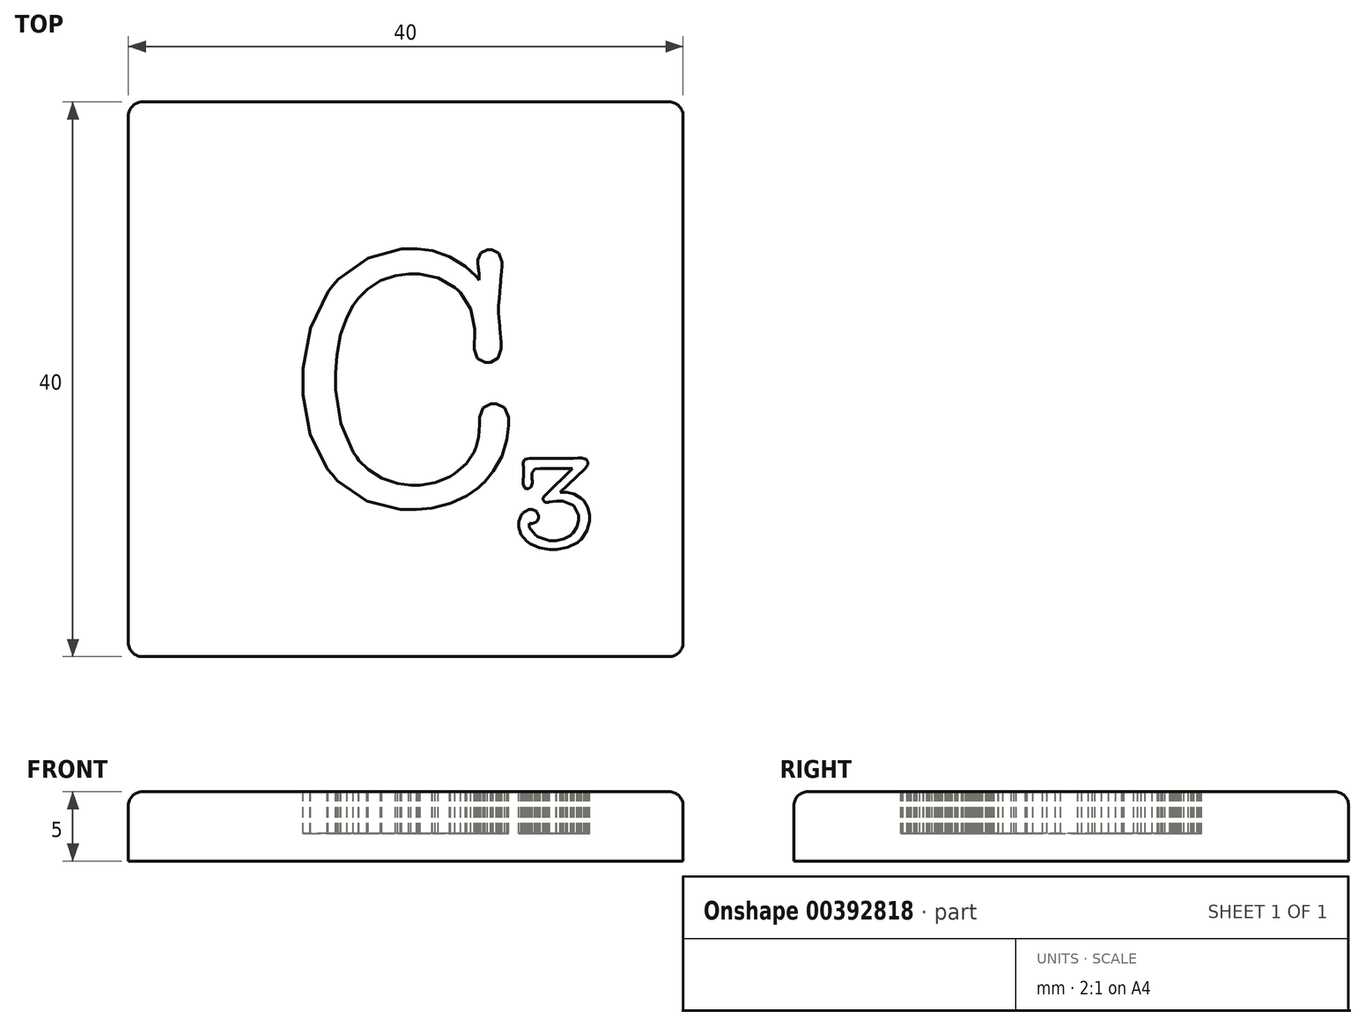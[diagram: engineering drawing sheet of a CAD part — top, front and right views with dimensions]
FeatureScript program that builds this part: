
annotation { "Feature Type Name" : "Feature", "Feature Type Description" : "" }
export const myFeature = defineFeature(function(context is Context, id is Id, definition is map)
    precondition{}
    {
        {
            var Q0;
            Q0=qCreatedBy(makeId("Top.planeOp"),FACE);
            var sketch = newSketch(context, id + "F0", { "sketchPlane" : qUnion([Q0])});
            skLineSegment(sketch, "E0.bottom", {"start": v(20, -20) * mm, "end": v(-20, -20) * mm});
            skLineSegment(sketch, "E0.top", {"start": v(20, 20) * mm, "end": v(-20, 20) * mm});
            skLineSegment(sketch, "E0.left", {"start": v(20, -20) * mm, "end": v(20, 20) * mm});
            skLineSegment(sketch, "E0.right", {"start": v(-20, -20) * mm, "end": v(-20, 20) * mm});
            skPoint(sketch, "E0.middle", {"position": v(0, 0) * mm});
            skSolve(sketch);
        }
        {
            var Q0;
            Q0=makeQuery(id+"F0.imprint","IMPRINT",FACE,{"disambiguationData":[TD([[makeQuery(id+"F0.imprint","IMPRINT",EDGE,{"derivedFrom":sQuery(id+"F0.wireOp",EDGE,"E0.bottom")}),-1.0]])]});
            extrude(context, id + "F1", {"entities" : qUnion([Q0]), "depth" : -5 * mm});
        }
        {
            var Q0;
            Q0=makeQuery(id+"F1.opExtrude","CAP_FACE",FACE,{"disambiguationData":[OSD([sQuery(id+"F0.wireOp",EDGE,"E0.bottom"),sQuery(id+"F0.wireOp",EDGE,"E0.top"),sQuery(id+"F0.wireOp",EDGE,"E0.left"),sQuery(id+"F0.wireOp",EDGE,"E0.right")])],"isStart":true});
            var Q1;
            Q1=makeQuery(id+"F1.opExtrude","SWEPT_EDGE",EDGE,{"disambiguationData":[OSD([sQuery(id+"F0.wireOp",EDGE,"E0.top"),sQuery(id+"F0.wireOp",EDGE,"E0.right")])]});
            var Q2;
            Q2=makeQuery(id+"F1.opExtrude","SWEPT_EDGE",EDGE,{"disambiguationData":[OSD([sQuery(id+"F0.wireOp",EDGE,"E0.top"),sQuery(id+"F0.wireOp",EDGE,"E0.left")])]});
            var Q3;
            Q3=makeQuery(id+"F1.opExtrude","SWEPT_EDGE",EDGE,{"disambiguationData":[OSD([sQuery(id+"F0.wireOp",EDGE,"E0.bottom"),sQuery(id+"F0.wireOp",EDGE,"E0.right")])]});
            var Q4;
            Q4=makeQuery(id+"F1.opExtrude","SWEPT_EDGE",EDGE,{"disambiguationData":[OSD([sQuery(id+"F0.wireOp",EDGE,"E0.bottom"),sQuery(id+"F0.wireOp",EDGE,"E0.left")])]});
            fillet(context, id + "F2", {"entities" : qUnion([Q0, Q1, Q2, Q3, Q4]), "radius" : 1 * mm, "tangentPropagation" : true, "allowEdgeOverflow" : false});
        }
        {
            var Q0;
            Q0=qCreatedBy(makeId("Top.planeOp"),FACE);
            var sketch = newSketch(context, id + "F3", { "sketchPlane" : qUnion([Q0])});
            skLineSegment(sketch, "E1", {"start": v(0.52, 9.4) * mm, "end": v(0.87, 9.4) * mm});
            skLineSegment(sketch, "E2", {"start": v(0.87, 9.4) * mm, "end": v(1.92, 9.27) * mm});
            skLineSegment(sketch, "E3", {"start": v(1.92, 9.27) * mm, "end": v(3.18, 8.84) * mm});
            skLineSegment(sketch, "E4", {"start": v(3.18, 8.84) * mm, "end": v(4.3, 8.14) * mm});
            skLineSegment(sketch, "E5", {"start": v(4.3, 8.14) * mm, "end": v(5.08, 7.43) * mm});
            skLineSegment(sketch, "E6", {"start": v(5.08, 7.43) * mm, "end": v(5.3, 7.16) * mm});
            skLineSegment(sketch, "E7", {"start": v(5.3, 7.16) * mm, "end": v(5.28, 7.45) * mm});
            skLineSegment(sketch, "E8", {"start": v(5.28, 7.45) * mm, "end": v(5.28, 7.74) * mm});
            skLineSegment(sketch, "E9", {"start": v(5.28, 7.74) * mm, "end": v(5.27, 7.77) * mm});
            skLineSegment(sketch, "E10", {"start": v(5.27, 7.77) * mm, "end": v(5.25, 7.89) * mm});
            skLineSegment(sketch, "E11", {"start": v(5.25, 7.89) * mm, "end": v(5.25, 7.92) * mm});
            skLineSegment(sketch, "E12", {"start": v(5.25, 7.92) * mm, "end": v(5.24, 8.02) * mm});
            skLineSegment(sketch, "E13", {"start": v(5.24, 8.02) * mm, "end": v(5.2, 8.45) * mm});
            skLineSegment(sketch, "E14", {"start": v(5.2, 8.45) * mm, "end": v(5.2, 8.62) * mm});
            skLineSegment(sketch, "E15", {"start": v(5.2, 8.62) * mm, "end": v(5.4, 9.13) * mm});
            skLineSegment(sketch, "E16", {"start": v(5.4, 9.13) * mm, "end": v(5.88, 9.35) * mm});
            skLineSegment(sketch, "E17", {"start": v(5.88, 9.35) * mm, "end": v(6.04, 9.35) * mm});
            skLineSegment(sketch, "E18", {"start": v(6.04, 9.35) * mm, "end": v(6.21, 9.35) * mm});
            skLineSegment(sketch, "E19", {"start": v(6.21, 9.35) * mm, "end": v(6.72, 9.08) * mm});
            skLineSegment(sketch, "E20", {"start": v(6.72, 9.08) * mm, "end": v(6.94, 8.45) * mm});
            skLineSegment(sketch, "E21", {"start": v(6.94, 8.45) * mm, "end": v(6.94, 8.24) * mm});
            skLineSegment(sketch, "E22", {"start": v(6.94, 8.24) * mm, "end": v(6.94, 8.14) * mm});
            skLineSegment(sketch, "E23", {"start": v(6.94, 8.14) * mm, "end": v(6.92, 7.82) * mm});
            skLineSegment(sketch, "E24", {"start": v(6.92, 7.82) * mm, "end": v(6.86, 7.15) * mm});
            skLineSegment(sketch, "E25", {"start": v(6.86, 7.15) * mm, "end": v(6.84, 6.97) * mm});
            skLineSegment(sketch, "E26", {"start": v(6.84, 6.97) * mm, "end": v(6.82, 6.75) * mm});
            skLineSegment(sketch, "E27", {"start": v(6.82, 6.75) * mm, "end": v(6.74, 5.85) * mm});
            skLineSegment(sketch, "E28", {"start": v(6.74, 5.85) * mm, "end": v(6.7, 5.32) * mm});
            skLineSegment(sketch, "E29", {"start": v(6.7, 5.32) * mm, "end": v(6.7, 5.15) * mm});
            skLineSegment(sketch, "E30", {"start": v(6.7, 5.15) * mm, "end": v(6.7, 4.78) * mm});
            skLineSegment(sketch, "E31", {"start": v(6.7, 4.78) * mm, "end": v(6.77, 3.82) * mm});
            skLineSegment(sketch, "E32", {"start": v(6.77, 3.82) * mm, "end": v(6.79, 3.7) * mm});
            skLineSegment(sketch, "E33", {"start": v(6.79, 3.7) * mm, "end": v(6.9, 2.69) * mm});
            skLineSegment(sketch, "E34", {"start": v(6.9, 2.69) * mm, "end": v(6.9, 2.42) * mm});
            skLineSegment(sketch, "E35", {"start": v(6.9, 2.42) * mm, "end": v(6.9, 2.2) * mm});
            skLineSegment(sketch, "E36", {"start": v(6.9, 2.2) * mm, "end": v(6.65, 1.53) * mm});
            skLineSegment(sketch, "E37", {"start": v(6.65, 1.53) * mm, "end": v(6.12, 1.23) * mm});
            skLineSegment(sketch, "E38", {"start": v(6.12, 1.23) * mm, "end": v(5.94, 1.23) * mm});
            skLineSegment(sketch, "E39", {"start": v(5.94, 1.23) * mm, "end": v(5.75, 1.23) * mm});
            skLineSegment(sketch, "E40", {"start": v(5.75, 1.23) * mm, "end": v(5.17, 1.52) * mm});
            skLineSegment(sketch, "E41", {"start": v(5.17, 1.52) * mm, "end": v(4.93, 2.18) * mm});
            skLineSegment(sketch, "E42", {"start": v(4.93, 2.18) * mm, "end": v(4.93, 2.37) * mm});
            skLineSegment(sketch, "E43", {"start": v(4.93, 2.37) * mm, "end": v(4.96, 3.32) * mm});
            skLineSegment(sketch, "E44", {"start": v(4.96, 3.32) * mm, "end": v(4.97, 3.64) * mm});
            skLineSegment(sketch, "E45", {"start": v(4.97, 3.64) * mm, "end": v(4.69, 5.05) * mm});
            skLineSegment(sketch, "E46", {"start": v(4.69, 5.05) * mm, "end": v(3.98, 6.22) * mm});
            skLineSegment(sketch, "E47", {"start": v(3.98, 6.22) * mm, "end": v(3.77, 6.42) * mm});
            skLineSegment(sketch, "E48", {"start": v(3.77, 6.42) * mm, "end": v(3.56, 6.61) * mm});
            skLineSegment(sketch, "E49", {"start": v(3.56, 6.61) * mm, "end": v(2.33, 7.3) * mm});
            skLineSegment(sketch, "E50", {"start": v(2.33, 7.3) * mm, "end": v(0.97, 7.6) * mm});
            skLineSegment(sketch, "E51", {"start": v(0.97, 7.6) * mm, "end": v(0.52, 7.6) * mm});
            skLineSegment(sketch, "E52", {"start": v(0.52, 7.6) * mm, "end": v(0.2, 7.6) * mm});
            skLineSegment(sketch, "E53", {"start": v(0.2, 7.6) * mm, "end": v(-0.72, 7.48) * mm});
            skLineSegment(sketch, "E54", {"start": v(-0.72, 7.48) * mm, "end": v(-1.82, 7.1) * mm});
            skLineSegment(sketch, "E55", {"start": v(-1.82, 7.1) * mm, "end": v(-2.77, 6.48) * mm});
            skLineSegment(sketch, "E56", {"start": v(-2.77, 6.48) * mm, "end": v(-3.4, 5.84) * mm});
            skLineSegment(sketch, "E57", {"start": v(-3.4, 5.84) * mm, "end": v(-3.58, 5.6) * mm});
            skLineSegment(sketch, "E58", {"start": v(-3.58, 5.6) * mm, "end": v(-3.77, 5.34) * mm});
            skLineSegment(sketch, "E59", {"start": v(-3.77, 5.34) * mm, "end": v(-4.23, 4.5) * mm});
            skLineSegment(sketch, "E60", {"start": v(-4.23, 4.5) * mm, "end": v(-4.7, 3.2) * mm});
            skLineSegment(sketch, "E61", {"start": v(-4.7, 3.2) * mm, "end": v(-4.98, 1.72) * mm});
            skLineSegment(sketch, "E62", {"start": v(-4.98, 1.72) * mm, "end": v(-5.07, 0.46) * mm});
            skLineSegment(sketch, "E63", {"start": v(-5.07, 0.46) * mm, "end": v(-5.07, 0.04) * mm});
            skLineSegment(sketch, "E64", {"start": v(-5.07, 0.04) * mm, "end": v(-5.07, -0.77) * mm});
            skLineSegment(sketch, "E65", {"start": v(-5.07, -0.77) * mm, "end": v(-4.69, -3.19) * mm});
            skLineSegment(sketch, "E66", {"start": v(-4.69, -3.19) * mm, "end": v(-3.8, -5.27) * mm});
            skLineSegment(sketch, "E67", {"start": v(-3.8, -5.27) * mm, "end": v(-3.55, -5.6) * mm});
            skLineSegment(sketch, "E68", {"start": v(-3.55, -5.6) * mm, "end": v(-3.37, -5.85) * mm});
            skLineSegment(sketch, "E69", {"start": v(-3.37, -5.85) * mm, "end": v(-2.71, -6.5) * mm});
            skLineSegment(sketch, "E70", {"start": v(-2.71, -6.5) * mm, "end": v(-1.72, -7.13) * mm});
            skLineSegment(sketch, "E71", {"start": v(-1.72, -7.13) * mm, "end": v(-0.59, -7.5) * mm});
            skLineSegment(sketch, "E72", {"start": v(-0.59, -7.5) * mm, "end": v(0.38, -7.63) * mm});
            skLineSegment(sketch, "E73", {"start": v(0.38, -7.63) * mm, "end": v(0.7, -7.63) * mm});
            skLineSegment(sketch, "E74", {"start": v(0.7, -7.63) * mm, "end": v(1.05, -7.63) * mm});
            skLineSegment(sketch, "E75", {"start": v(1.05, -7.63) * mm, "end": v(2.1, -7.45) * mm});
            skLineSegment(sketch, "E76", {"start": v(2.1, -7.45) * mm, "end": v(3.16, -7.04) * mm});
            skLineSegment(sketch, "E77", {"start": v(3.16, -7.04) * mm, "end": v(3.36, -6.92) * mm});
            skLineSegment(sketch, "E78", {"start": v(3.36, -6.92) * mm, "end": v(3.56, -6.8) * mm});
            skLineSegment(sketch, "E79", {"start": v(3.56, -6.8) * mm, "end": v(4.36, -6.1) * mm});
            skLineSegment(sketch, "E80", {"start": v(4.36, -6.1) * mm, "end": v(4.93, -5.23) * mm});
            skLineSegment(sketch, "E81", {"start": v(4.93, -5.23) * mm, "end": v(5.01, -5.04) * mm});
            skLineSegment(sketch, "E82", {"start": v(5.01, -5.04) * mm, "end": v(5.07, -4.91) * mm});
            skLineSegment(sketch, "E83", {"start": v(5.07, -4.91) * mm, "end": v(5.25, -4.14) * mm});
            skLineSegment(sketch, "E84", {"start": v(5.25, -4.14) * mm, "end": v(5.33, -3.27) * mm});
            skLineSegment(sketch, "E85", {"start": v(5.33, -3.27) * mm, "end": v(5.33, -2.98) * mm});
            skLineSegment(sketch, "E86", {"start": v(5.33, -2.98) * mm, "end": v(5.33, -2.75) * mm});
            skLineSegment(sketch, "E87", {"start": v(5.33, -2.75) * mm, "end": v(5.58, -2.06) * mm});
            skLineSegment(sketch, "E88", {"start": v(5.58, -2.06) * mm, "end": v(6.15, -1.76) * mm});
            skLineSegment(sketch, "E89", {"start": v(6.15, -1.76) * mm, "end": v(6.34, -1.76) * mm});
            skLineSegment(sketch, "E90", {"start": v(6.34, -1.76) * mm, "end": v(6.54, -1.76) * mm});
            skLineSegment(sketch, "E91", {"start": v(6.54, -1.76) * mm, "end": v(7.15, -2.06) * mm});
            skLineSegment(sketch, "E92", {"start": v(7.15, -2.06) * mm, "end": v(7.42, -2.75) * mm});
            skLineSegment(sketch, "E93", {"start": v(7.42, -2.75) * mm, "end": v(7.42, -2.98) * mm});
            skLineSegment(sketch, "E94", {"start": v(7.42, -2.98) * mm, "end": v(7.42, -3.31) * mm});
            skLineSegment(sketch, "E95", {"start": v(7.42, -3.31) * mm, "end": v(7.3, -4.33) * mm});
            skLineSegment(sketch, "E96", {"start": v(7.3, -4.33) * mm, "end": v(6.93, -5.55) * mm});
            skLineSegment(sketch, "E97", {"start": v(6.93, -5.55) * mm, "end": v(6.32, -6.64) * mm});
            skLineSegment(sketch, "E98", {"start": v(6.32, -6.64) * mm, "end": v(5.7, -7.39) * mm});
            skLineSegment(sketch, "E99", {"start": v(5.7, -7.39) * mm, "end": v(5.46, -7.6) * mm});
            skLineSegment(sketch, "E100", {"start": v(5.46, -7.6) * mm, "end": v(5.22, -7.83) * mm});
            skLineSegment(sketch, "E101", {"start": v(5.22, -7.83) * mm, "end": v(4.41, -8.4) * mm});
            skLineSegment(sketch, "E102", {"start": v(4.41, -8.4) * mm, "end": v(3.22, -8.96) * mm});
            skLineSegment(sketch, "E103", {"start": v(3.22, -8.96) * mm, "end": v(1.89, -9.3) * mm});
            skLineSegment(sketch, "E104", {"start": v(1.89, -9.3) * mm, "end": v(0.78, -9.4) * mm});
            skLineSegment(sketch, "E105", {"start": v(0.78, -9.4) * mm, "end": v(0.4, -9.4) * mm});
            skLineSegment(sketch, "E106", {"start": v(0.4, -9.4) * mm, "end": v(-0.4, -9.4) * mm});
            skLineSegment(sketch, "E107", {"start": v(-0.4, -9.4) * mm, "end": v(-2.8, -8.78) * mm});
            skLineSegment(sketch, "E108", {"start": v(-2.8, -8.78) * mm, "end": v(-4.94, -7.31) * mm});
            skLineSegment(sketch, "E109", {"start": v(-4.94, -7.31) * mm, "end": v(-5.3, -6.9) * mm});
            skLineSegment(sketch, "E110", {"start": v(-5.3, -6.9) * mm, "end": v(-5.65, -6.47) * mm});
            skLineSegment(sketch, "E111", {"start": v(-5.65, -6.47) * mm, "end": v(-6.89, -3.96) * mm});
            skLineSegment(sketch, "E112", {"start": v(-6.89, -3.96) * mm, "end": v(-7.42, -1.14) * mm});
            skLineSegment(sketch, "E113", {"start": v(-7.42, -1.14) * mm, "end": v(-7.42, -0.2) * mm});
            skLineSegment(sketch, "E114", {"start": v(-7.42, -0.2) * mm, "end": v(-7.42, 0.78) * mm});
            skLineSegment(sketch, "E115", {"start": v(-7.42, 0.78) * mm, "end": v(-6.88, 3.7) * mm});
            skLineSegment(sketch, "E116", {"start": v(-6.88, 3.7) * mm, "end": v(-5.6, 6.32) * mm});
            skLineSegment(sketch, "E117", {"start": v(-5.6, 6.32) * mm, "end": v(-5.24, 6.76) * mm});
            skLineSegment(sketch, "E118", {"start": v(-5.24, 6.76) * mm, "end": v(-4.87, 7.2) * mm});
            skLineSegment(sketch, "E119", {"start": v(-4.87, 7.2) * mm, "end": v(-2.7, 8.74) * mm});
            skLineSegment(sketch, "E120", {"start": v(-2.7, 8.74) * mm, "end": v(-0.3, 9.4) * mm});
            skLineSegment(sketch, "E121", {"start": v(-0.3, 9.4) * mm, "end": v(0.52, 9.4) * mm});
            skSolve(sketch);
        }
        {
            var Q0;
            Q0=qCreatedBy(makeId("Top.planeOp"),FACE);
            var sketch = newSketch(context, id + "F4", { "sketchPlane" : qUnion([Q0])});
            skLineSegment(sketch, "E122", {"start": v(10.05, -8.37) * mm, "end": v(12.03, -6.43) * mm});
            skLineSegment(sketch, "E123", {"start": v(12.03, -6.43) * mm, "end": v(9.82, -6.43) * mm});
            skLineSegment(sketch, "E124", {"start": v(9.82, -6.43) * mm, "end": v(9.7, -6.43) * mm});
            skLineSegment(sketch, "E125", {"start": v(9.7, -6.43) * mm, "end": v(9.35, -6.47) * mm});
            skLineSegment(sketch, "E126", {"start": v(9.35, -6.47) * mm, "end": v(9.33, -6.48) * mm});
            skLineSegment(sketch, "E127", {"start": v(9.33, -6.48) * mm, "end": v(9.29, -6.5) * mm});
            skLineSegment(sketch, "E128", {"start": v(9.29, -6.5) * mm, "end": v(9.09, -6.76) * mm});
            skLineSegment(sketch, "E129", {"start": v(9.09, -6.76) * mm, "end": v(9.09, -6.85) * mm});
            skLineSegment(sketch, "E130", {"start": v(9.09, -6.85) * mm, "end": v(9.09, -6.92) * mm});
            skLineSegment(sketch, "E131", {"start": v(9.09, -6.92) * mm, "end": v(9.1, -7.1) * mm});
            skLineSegment(sketch, "E132", {"start": v(9.1, -7.1) * mm, "end": v(9.1, -7.13) * mm});
            skLineSegment(sketch, "E133", {"start": v(9.1, -7.13) * mm, "end": v(9.11, -7.15) * mm});
            skLineSegment(sketch, "E134", {"start": v(9.11, -7.15) * mm, "end": v(9.13, -7.34) * mm});
            skLineSegment(sketch, "E135", {"start": v(9.13, -7.34) * mm, "end": v(9.13, -7.4) * mm});
            skLineSegment(sketch, "E136", {"start": v(9.13, -7.4) * mm, "end": v(9.13, -7.5) * mm});
            skLineSegment(sketch, "E137", {"start": v(9.13, -7.5) * mm, "end": v(9.04, -7.77) * mm});
            skLineSegment(sketch, "E138", {"start": v(9.04, -7.77) * mm, "end": v(8.86, -7.9) * mm});
            skLineSegment(sketch, "E139", {"start": v(8.86, -7.9) * mm, "end": v(8.8, -7.9) * mm});
            skLineSegment(sketch, "E140", {"start": v(8.8, -7.9) * mm, "end": v(8.73, -7.9) * mm});
            skLineSegment(sketch, "E141", {"start": v(8.73, -7.9) * mm, "end": v(8.55, -7.8) * mm});
            skLineSegment(sketch, "E142", {"start": v(8.55, -7.8) * mm, "end": v(8.47, -7.56) * mm});
            skLineSegment(sketch, "E143", {"start": v(8.47, -7.56) * mm, "end": v(8.47, -7.49) * mm});
            skLineSegment(sketch, "E144", {"start": v(8.47, -7.49) * mm, "end": v(8.47, -7.4) * mm});
            skLineSegment(sketch, "E145", {"start": v(8.47, -7.4) * mm, "end": v(8.48, -7.18) * mm});
            skLineSegment(sketch, "E146", {"start": v(8.48, -7.18) * mm, "end": v(8.48, -7.14) * mm});
            skLineSegment(sketch, "E147", {"start": v(8.48, -7.14) * mm, "end": v(8.49, -7.1) * mm});
            skLineSegment(sketch, "E148", {"start": v(8.49, -7.1) * mm, "end": v(8.5, -6.8) * mm});
            skLineSegment(sketch, "E149", {"start": v(8.5, -6.8) * mm, "end": v(8.5, -6.7) * mm});
            skLineSegment(sketch, "E150", {"start": v(8.5, -6.7) * mm, "end": v(8.5, -6.41) * mm});
            skLineSegment(sketch, "E151", {"start": v(8.5, -6.41) * mm, "end": v(8.49, -6.4) * mm});
            skLineSegment(sketch, "E152", {"start": v(8.49, -6.4) * mm, "end": v(8.49, -6.37) * mm});
            skLineSegment(sketch, "E153", {"start": v(8.49, -6.37) * mm, "end": v(8.48, -6.16) * mm});
            skLineSegment(sketch, "E154", {"start": v(8.48, -6.16) * mm, "end": v(8.48, -6.1) * mm});
            skLineSegment(sketch, "E155", {"start": v(8.48, -6.1) * mm, "end": v(8.48, -6.02) * mm});
            skLineSegment(sketch, "E156", {"start": v(8.48, -6.02) * mm, "end": v(8.56, -5.79) * mm});
            skLineSegment(sketch, "E157", {"start": v(8.56, -5.79) * mm, "end": v(8.58, -5.78) * mm});
            skLineSegment(sketch, "E158", {"start": v(8.58, -5.78) * mm, "end": v(8.6, -5.77) * mm});
            skLineSegment(sketch, "E159", {"start": v(8.6, -5.77) * mm, "end": v(8.94, -5.72) * mm});
            skLineSegment(sketch, "E160", {"start": v(8.94, -5.72) * mm, "end": v(9.05, -5.72) * mm});
            skLineSegment(sketch, "E161", {"start": v(9.05, -5.72) * mm, "end": v(11.4, -5.72) * mm});
            skLineSegment(sketch, "E162", {"start": v(11.4, -5.72) * mm, "end": v(11.56, -5.72) * mm});
            skLineSegment(sketch, "E163", {"start": v(11.56, -5.72) * mm, "end": v(11.97, -5.7) * mm});
            skLineSegment(sketch, "E164", {"start": v(11.97, -5.7) * mm, "end": v(12.04, -5.7) * mm});
            skLineSegment(sketch, "E165", {"start": v(12.04, -5.7) * mm, "end": v(12.08, -5.7) * mm});
            skLineSegment(sketch, "E166", {"start": v(12.08, -5.7) * mm, "end": v(12.45, -5.69) * mm});
            skLineSegment(sketch, "E167", {"start": v(12.45, -5.69) * mm, "end": v(12.58, -5.69) * mm});
            skLineSegment(sketch, "E168", {"start": v(12.58, -5.69) * mm, "end": v(12.68, -5.69) * mm});
            skLineSegment(sketch, "E169", {"start": v(12.68, -5.69) * mm, "end": v(13, -5.77) * mm});
            skLineSegment(sketch, "E170", {"start": v(13, -5.77) * mm, "end": v(13.14, -5.97) * mm});
            skLineSegment(sketch, "E171", {"start": v(13.14, -5.97) * mm, "end": v(13.14, -6.03) * mm});
            skLineSegment(sketch, "E172", {"start": v(13.14, -6.03) * mm, "end": v(13.14, -6.14) * mm});
            skLineSegment(sketch, "E173", {"start": v(13.14, -6.14) * mm, "end": v(12.94, -6.44) * mm});
            skLineSegment(sketch, "E174", {"start": v(12.94, -6.44) * mm, "end": v(12.9, -6.48) * mm});
            skLineSegment(sketch, "E175", {"start": v(12.9, -6.48) * mm, "end": v(11.15, -8.16) * mm});
            skLineSegment(sketch, "E176", {"start": v(11.15, -8.16) * mm, "end": v(11.18, -8.16) * mm});
            skLineSegment(sketch, "E177", {"start": v(11.18, -8.16) * mm, "end": v(11.28, -8.16) * mm});
            skLineSegment(sketch, "E178", {"start": v(11.28, -8.16) * mm, "end": v(11.3, -8.15) * mm});
            skLineSegment(sketch, "E179", {"start": v(11.3, -8.15) * mm, "end": v(11.42, -8.15) * mm});
            skLineSegment(sketch, "E180", {"start": v(11.42, -8.15) * mm, "end": v(11.6, -8.15) * mm});
            skLineSegment(sketch, "E181", {"start": v(11.6, -8.15) * mm, "end": v(12.16, -8.28) * mm});
            skLineSegment(sketch, "E182", {"start": v(12.16, -8.28) * mm, "end": v(12.67, -8.59) * mm});
            skLineSegment(sketch, "E183", {"start": v(12.67, -8.59) * mm, "end": v(12.75, -8.67) * mm});
            skLineSegment(sketch, "E184", {"start": v(12.75, -8.67) * mm, "end": v(12.84, -8.76) * mm});
            skLineSegment(sketch, "E185", {"start": v(12.84, -8.76) * mm, "end": v(13.14, -9.26) * mm});
            skLineSegment(sketch, "E186", {"start": v(13.14, -9.26) * mm, "end": v(13.27, -9.82) * mm});
            skLineSegment(sketch, "E187", {"start": v(13.27, -9.82) * mm, "end": v(13.27, -10) * mm});
            skLineSegment(sketch, "E188", {"start": v(13.27, -10) * mm, "end": v(13.27, -10.23) * mm});
            skLineSegment(sketch, "E189", {"start": v(13.27, -10.23) * mm, "end": v(13.09, -10.92) * mm});
            skLineSegment(sketch, "E190", {"start": v(13.09, -10.92) * mm, "end": v(12.66, -11.54) * mm});
            skLineSegment(sketch, "E191", {"start": v(12.66, -11.54) * mm, "end": v(12.53, -11.65) * mm});
            skLineSegment(sketch, "E192", {"start": v(12.53, -11.65) * mm, "end": v(12.4, -11.76) * mm});
            skLineSegment(sketch, "E193", {"start": v(12.4, -11.76) * mm, "end": v(11.69, -12.13) * mm});
            skLineSegment(sketch, "E194", {"start": v(11.69, -12.13) * mm, "end": v(10.9, -12.29) * mm});
            skLineSegment(sketch, "E195", {"start": v(10.9, -12.29) * mm, "end": v(10.63, -12.29) * mm});
            skLineSegment(sketch, "E196", {"start": v(10.63, -12.29) * mm, "end": v(10.39, -12.29) * mm});
            skLineSegment(sketch, "E197", {"start": v(10.39, -12.29) * mm, "end": v(9.65, -12.16) * mm});
            skLineSegment(sketch, "E198", {"start": v(9.65, -12.16) * mm, "end": v(8.97, -11.85) * mm});
            skLineSegment(sketch, "E199", {"start": v(8.97, -11.85) * mm, "end": v(8.85, -11.77) * mm});
            skLineSegment(sketch, "E200", {"start": v(8.85, -11.77) * mm, "end": v(8.73, -11.68) * mm});
            skLineSegment(sketch, "E201", {"start": v(8.73, -11.68) * mm, "end": v(8.32, -11.18) * mm});
            skLineSegment(sketch, "E202", {"start": v(8.32, -11.18) * mm, "end": v(8.14, -10.65) * mm});
            skLineSegment(sketch, "E203", {"start": v(8.14, -10.65) * mm, "end": v(8.14, -10.47) * mm});
            skLineSegment(sketch, "E204", {"start": v(8.14, -10.47) * mm, "end": v(8.14, -10.28) * mm});
            skLineSegment(sketch, "E205", {"start": v(8.14, -10.28) * mm, "end": v(8.35, -9.76) * mm});
            skLineSegment(sketch, "E206", {"start": v(8.35, -9.76) * mm, "end": v(8.4, -9.71) * mm});
            skLineSegment(sketch, "E207", {"start": v(8.4, -9.71) * mm, "end": v(8.44, -9.66) * mm});
            skLineSegment(sketch, "E208", {"start": v(8.44, -9.66) * mm, "end": v(8.88, -9.4) * mm});
            skLineSegment(sketch, "E209", {"start": v(8.88, -9.4) * mm, "end": v(9.03, -9.4) * mm});
            skLineSegment(sketch, "E210", {"start": v(9.03, -9.4) * mm, "end": v(9.13, -9.4) * mm});
            skLineSegment(sketch, "E211", {"start": v(9.13, -9.4) * mm, "end": v(9.41, -9.52) * mm});
            skLineSegment(sketch, "E212", {"start": v(9.41, -9.52) * mm, "end": v(9.44, -9.55) * mm});
            skLineSegment(sketch, "E213", {"start": v(9.44, -9.55) * mm, "end": v(9.46, -9.57) * mm});
            skLineSegment(sketch, "E214", {"start": v(9.46, -9.57) * mm, "end": v(9.6, -9.84) * mm});
            skLineSegment(sketch, "E215", {"start": v(9.6, -9.84) * mm, "end": v(9.6, -9.94) * mm});
            skLineSegment(sketch, "E216", {"start": v(9.6, -9.94) * mm, "end": v(9.6, -10.02) * mm});
            skLineSegment(sketch, "E217", {"start": v(9.6, -10.02) * mm, "end": v(9.45, -10.3) * mm});
            skLineSegment(sketch, "E218", {"start": v(9.45, -10.3) * mm, "end": v(9.14, -10.41) * mm});
            skLineSegment(sketch, "E219", {"start": v(9.14, -10.41) * mm, "end": v(9.03, -10.41) * mm});
            skLineSegment(sketch, "E220", {"start": v(9.03, -10.41) * mm, "end": v(8.93, -10.41) * mm});
            skLineSegment(sketch, "E221", {"start": v(8.93, -10.41) * mm, "end": v(8.93, -10.48) * mm});
            skLineSegment(sketch, "E222", {"start": v(8.93, -10.48) * mm, "end": v(8.93, -10.68) * mm});
            skLineSegment(sketch, "E223", {"start": v(8.93, -10.68) * mm, "end": v(9.36, -11.23) * mm});
            skLineSegment(sketch, "E224", {"start": v(9.36, -11.23) * mm, "end": v(9.45, -11.29) * mm});
            skLineSegment(sketch, "E225", {"start": v(9.45, -11.29) * mm, "end": v(9.53, -11.34) * mm});
            skLineSegment(sketch, "E226", {"start": v(9.53, -11.34) * mm, "end": v(10.39, -11.63) * mm});
            skLineSegment(sketch, "E227", {"start": v(10.39, -11.63) * mm, "end": v(10.67, -11.63) * mm});
            skLineSegment(sketch, "E228", {"start": v(10.67, -11.63) * mm, "end": v(10.85, -11.63) * mm});
            skLineSegment(sketch, "E229", {"start": v(10.85, -11.63) * mm, "end": v(11.39, -11.52) * mm});
            skLineSegment(sketch, "E230", {"start": v(11.39, -11.52) * mm, "end": v(11.88, -11.25) * mm});
            skLineSegment(sketch, "E231", {"start": v(11.88, -11.25) * mm, "end": v(11.97, -11.18) * mm});
            skLineSegment(sketch, "E232", {"start": v(11.97, -11.18) * mm, "end": v(12.05, -11.1) * mm});
            skLineSegment(sketch, "E233", {"start": v(12.05, -11.1) * mm, "end": v(12.34, -10.66) * mm});
            skLineSegment(sketch, "E234", {"start": v(12.34, -10.66) * mm, "end": v(12.47, -10.18) * mm});
            skLineSegment(sketch, "E235", {"start": v(12.47, -10.18) * mm, "end": v(12.47, -10.02) * mm});
            skLineSegment(sketch, "E236", {"start": v(12.47, -10.02) * mm, "end": v(12.47, -9.79) * mm});
            skLineSegment(sketch, "E237", {"start": v(12.47, -9.79) * mm, "end": v(12.12, -9.1) * mm});
            skLineSegment(sketch, "E238", {"start": v(12.12, -9.1) * mm, "end": v(11.32, -8.78) * mm});
            skLineSegment(sketch, "E239", {"start": v(11.32, -8.78) * mm, "end": v(11.06, -8.78) * mm});
            skLineSegment(sketch, "E240", {"start": v(11.06, -8.78) * mm, "end": v(10.87, -8.78) * mm});
            skLineSegment(sketch, "E241", {"start": v(10.87, -8.78) * mm, "end": v(10.36, -8.85) * mm});
            skLineSegment(sketch, "E242", {"start": v(10.36, -8.85) * mm, "end": v(10.3, -8.87) * mm});
            skLineSegment(sketch, "E243", {"start": v(10.3, -8.87) * mm, "end": v(10.27, -8.87) * mm});
            skLineSegment(sketch, "E244", {"start": v(10.27, -8.87) * mm, "end": v(10.16, -8.89) * mm});
            skLineSegment(sketch, "E245", {"start": v(10.16, -8.89) * mm, "end": v(10.13, -8.89) * mm});
            skLineSegment(sketch, "E246", {"start": v(10.13, -8.89) * mm, "end": v(10.07, -8.89) * mm});
            skLineSegment(sketch, "E247", {"start": v(10.07, -8.89) * mm, "end": v(9.9, -8.7) * mm});
            skLineSegment(sketch, "E248", {"start": v(9.9, -8.7) * mm, "end": v(9.9, -8.64) * mm});
            skLineSegment(sketch, "E249", {"start": v(9.9, -8.64) * mm, "end": v(9.9, -8.57) * mm});
            skLineSegment(sketch, "E250", {"start": v(9.9, -8.57) * mm, "end": v(10.03, -8.4) * mm});
            skLineSegment(sketch, "E251", {"start": v(10.03, -8.4) * mm, "end": v(10.05, -8.37) * mm});
            skSolve(sketch);
        }
        {
            var Q0;
            Q0 = qSketchRegion(id + "F3", true);
            var Q1;
            Q1 = qSketchRegion(id + "F4", true);
            extrude(context, id + "F5", {"entities" : qUnion([Q0, Q1]), "depth" : -3 * mm});
        }
    });
